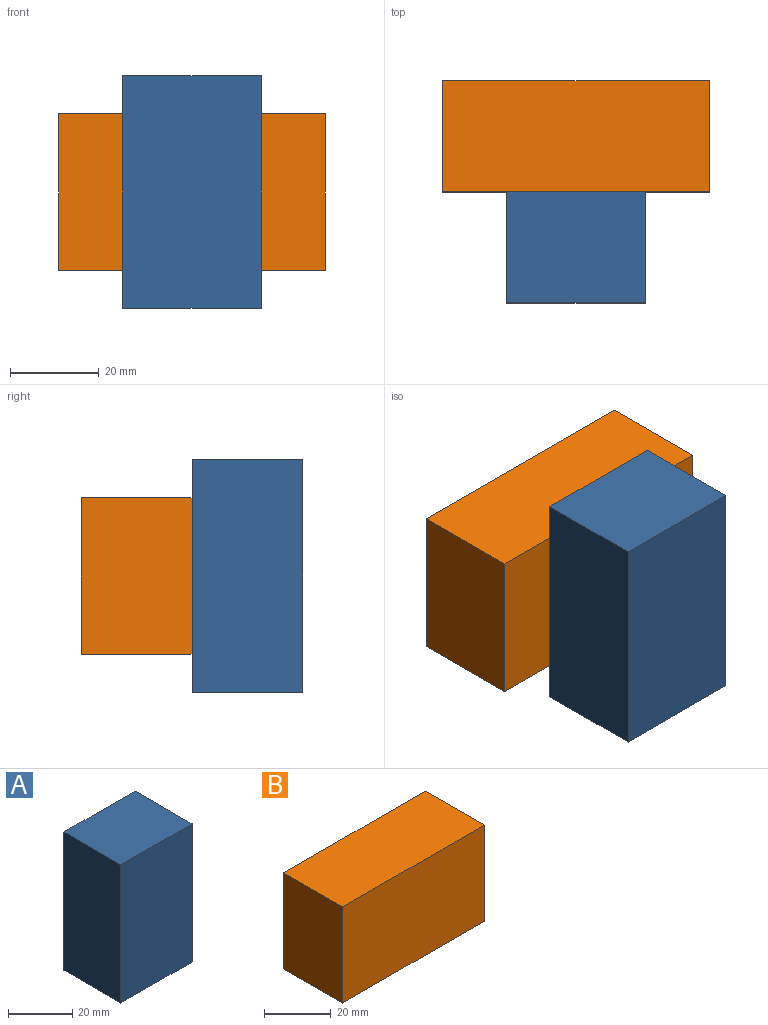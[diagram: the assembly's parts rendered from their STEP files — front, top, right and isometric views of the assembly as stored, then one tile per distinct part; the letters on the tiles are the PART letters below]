
ASSEMBLY  parts=2 mates=1
PART A: 6 faces, bbox 31.2x25x52.5 mm
  f0: plane 31.18x25mm, normal (0,0,1), area 779.6mm2, adj f1,f3,f4,f5
  f1: plane 52.47x25mm, normal (-1,0,0), area 1311.8mm2, adj f0,f2,f4,f5
  f2: plane 31.18x25mm, normal (0,0,-1), area 779.6mm2, adj f1,f3,f4,f5
  f3: plane 52.47x25mm, normal (1,0,0), area 1311.8mm2, adj f0,f2,f4,f5
  f4: plane 52.47x31.18mm, normal (0,-1,0), area 1636.3mm2, adj f0,f1,f2,f3
  f5: plane 52.47x31.18mm, normal (0,1,0), area 1636.3mm2, adj f0,f1,f2,f3
PART B: 6 faces, bbox 60.1x25x35.2 mm
  f0: plane 60.07x25mm, normal (0,0,1), area 1501.7mm2, adj f1,f3,f4,f5
  f1: plane 35.23x25mm, normal (-1,0,0), area 880.7mm2, adj f0,f2,f4,f5
  f2: plane 60.07x25mm, normal (0,0,-1), area 1501.7mm2, adj f1,f3,f4,f5
  f3: plane 35.23x25mm, normal (1,0,0), area 880.7mm2, adj f0,f2,f4,f5
  f4: plane 60.07x35.23mm, normal (0,-1,0), area 2116.2mm2, adj f0,f1,f2,f3
  f5: plane 60.07x35.23mm, normal (0,1,0), area 2116.2mm2, adj f0,f1,f2,f3
PLACE A rot(axis=(1,0,0),180deg) t=(91.77,-50,2.63)mm
PLACE B at identity
MATE revolute A.f4 <-> B.f4  axis (0,1,0) through (34.34,-25,-23.61)mm
